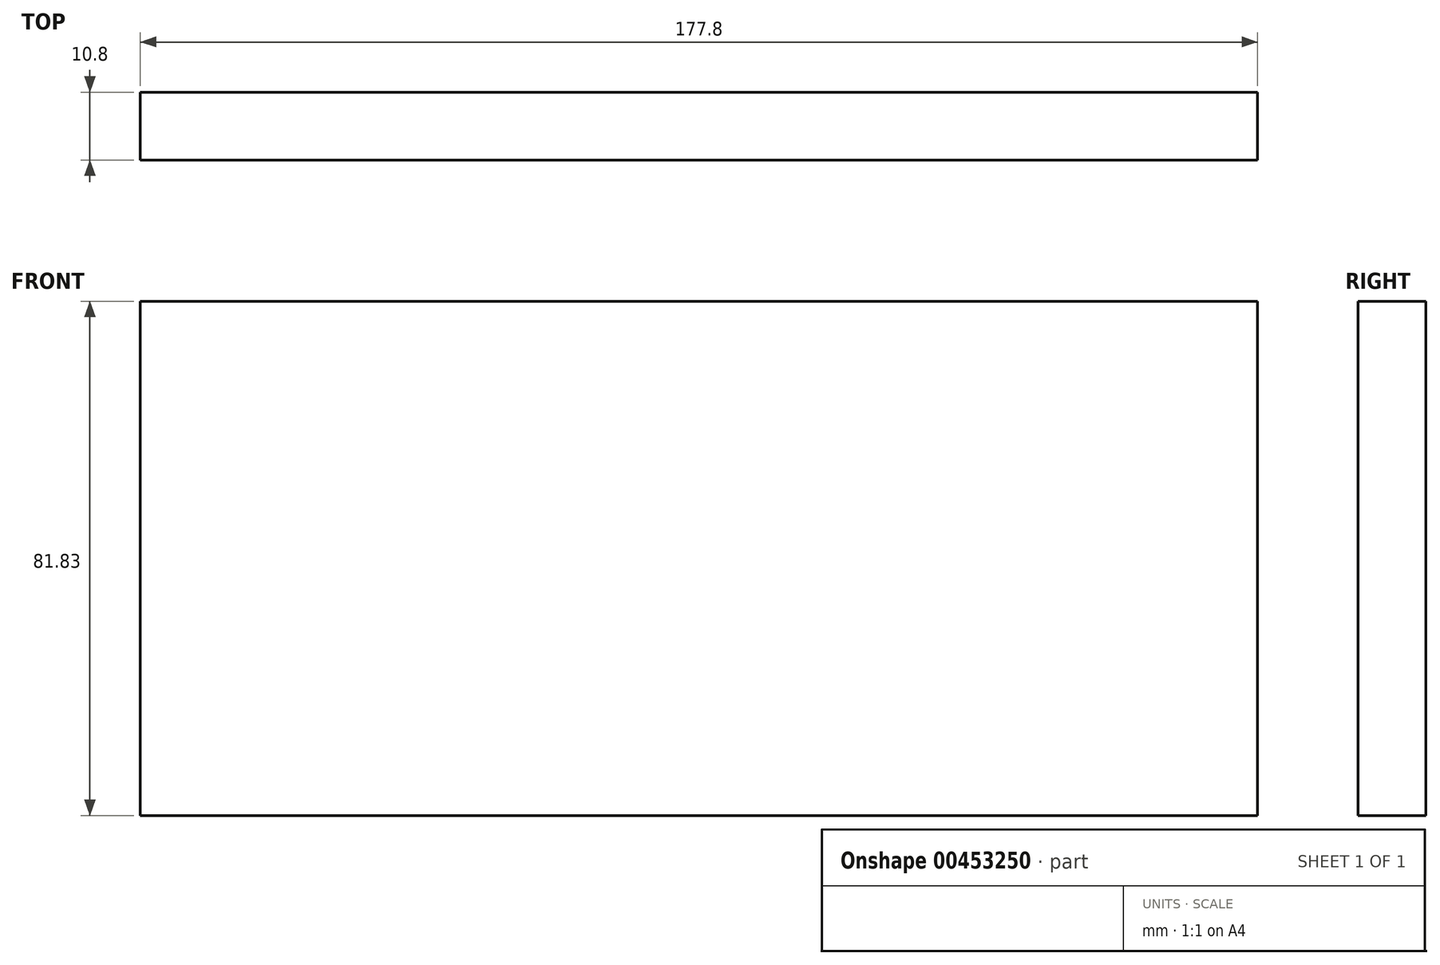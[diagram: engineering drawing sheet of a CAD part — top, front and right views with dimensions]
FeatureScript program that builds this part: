
annotation { "Feature Type Name" : "Feature", "Feature Type Description" : "" }
export const myFeature = defineFeature(function(context is Context, id is Id, definition is map)
    precondition{}
    {
        {
            var Q0;
            Q0=qCreatedBy(makeId("Front.planeOp"),FACE);
            var sketch = newSketch(context, id + "F0", { "sketchPlane" : qUnion([Q0])});
            skLineSegment(sketch, "E0.bottom", {"start": v(-81.26, 38.78) * mm, "end": v(96.54, 38.78) * mm});
            skLineSegment(sketch, "E0.top", {"start": v(-81.26, -43.05) * mm, "end": v(96.54, -43.05) * mm});
            skLineSegment(sketch, "E0.left", {"start": v(-81.26, 38.78) * mm, "end": v(-81.26, -43.05) * mm});
            skLineSegment(sketch, "E0.right", {"start": v(96.54, 38.78) * mm, "end": v(96.54, -43.05) * mm});
            skSolve(sketch);
        }
        {
            var Q0;
            Q0 = qSketchRegion(id + "F0", true);
            extrude(context, id + "F1", {"entities" : qUnion([Q0]), "depth" : 10.8 * mm});
        }
    });
